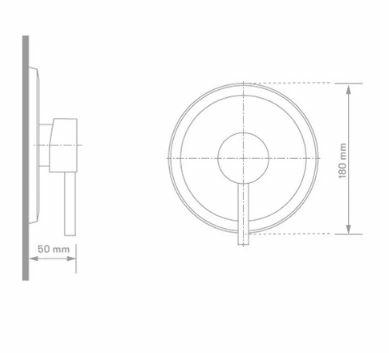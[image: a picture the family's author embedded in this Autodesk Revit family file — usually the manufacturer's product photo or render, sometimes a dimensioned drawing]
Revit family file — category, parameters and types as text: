
# Revit family: 01-2101-11SR-DUCHA MONOMANDO SST SIN REGADERA VIVALDI
name_source: partatom
category: Aparatos sanitarios
revit_build: Autodesk Revit 2018 (Build: 20170223_1515(x64)
units: mm (PartAtom-declared; Revit-internal decimal feet)

## family parameters
Anfitrión = Cara
Compartido = No
Corte con vacíos al cargar = No
Cota de conector redondo = Diámetro de uso
Número OmniClass = 23.31.11.00
Punto de cálculo de habitación = No
Tipo de pieza = Normal

## types (1)
- 01-2101-11SR
    Conexión AC = Sí
    Conexión AF = Sí
    Conexión de residuos = No
    Conexión de ventilación = No
    Descripción = Griferia Monomando Ducha
    Diametro = 180 mm
    Elevación por defecto = 0 mm  [stored 0 ft]
    Fabricante = Gricol
    Imagen de tipo = <Ninguno>
    Link Ficha Tecnica = https://infotecnica.gricol.com
    Modelo = 01-2101-11SR
    Plastico ABS Cromado = Plastico ABS Cromado
    Product Name = DUCHA MONOMANDO SST SIN REGADERA VIVALDI
    Profundidad = 50 mm  [stored 0.164042 ft]
    URL = https://www.gricol.com

note: [stored X ft] marks values corroborated as IEEE doubles in the binary element streams (Revit-internal decimal feet)

## geometry (parser evidence)
native form markers: Blend x2, Sweep x3
no freeform markers — native parametric forms only
